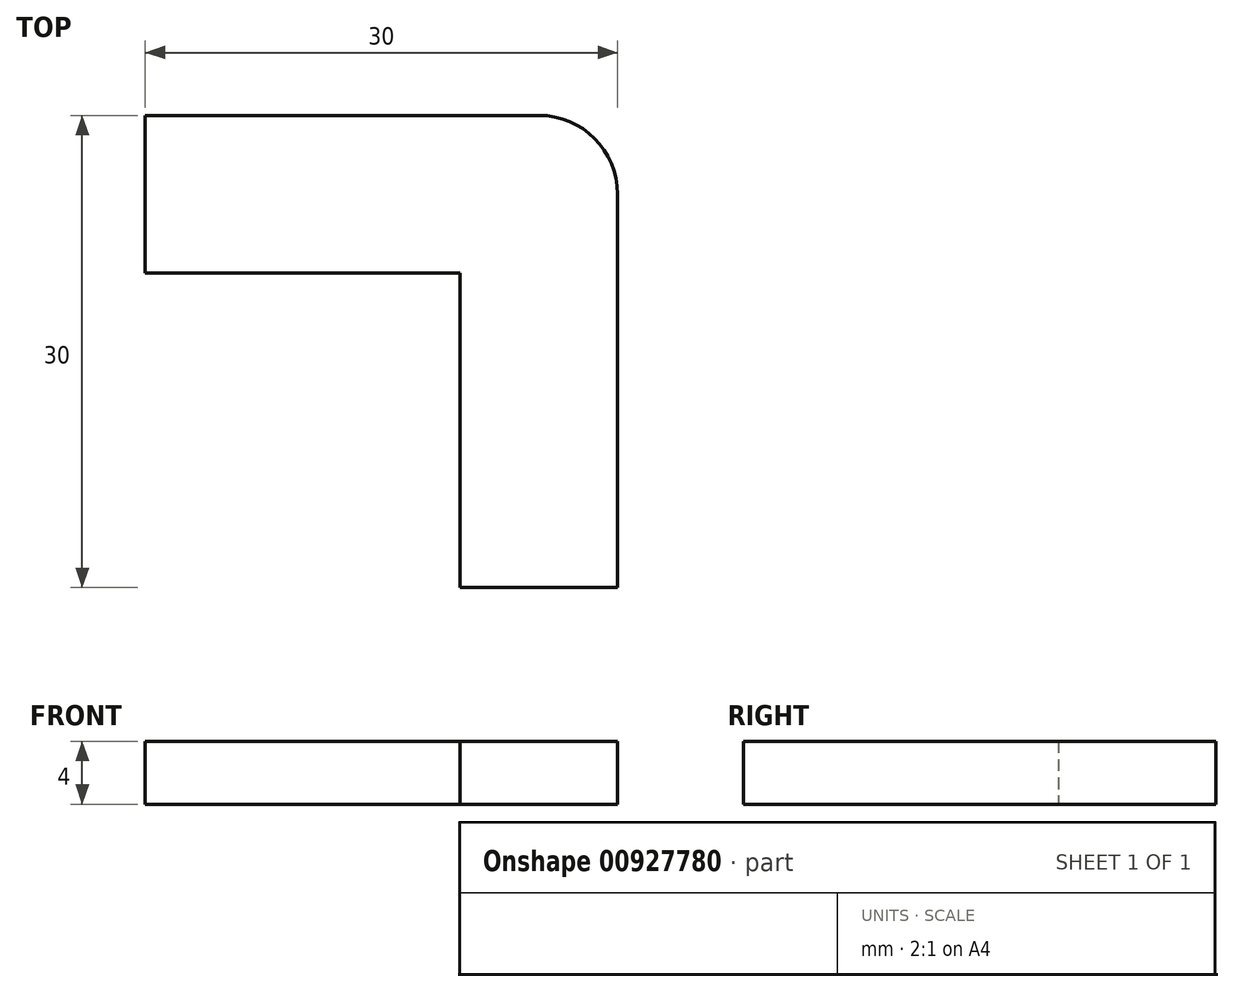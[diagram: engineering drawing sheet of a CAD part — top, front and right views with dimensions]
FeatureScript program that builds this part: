
annotation { "Feature Type Name" : "Feature", "Feature Type Description" : "" }
export const myFeature = defineFeature(function(context is Context, id is Id, definition is map)
    precondition{}
    {
        {
            var Q0;
            Q0=qCreatedBy(makeId("Top.planeOp"),FACE);
            var sketch = newSketch(context, id + "F0", { "sketchPlane" : qUnion([Q0])});
            skLineSegment(sketch, "E0.bottom", {"start": v(5, 15) * mm, "end": v(-5, 15) * mm});
            skLineSegment(sketch, "E0.top", {"start": v(5, -15) * mm, "end": v(-5, -15) * mm});
            skLineSegment(sketch, "E0.left", {"start": v(5, 15) * mm, "end": v(5, -15) * mm});
            skLineSegment(sketch, "E0.right", {"start": v(-5, 15) * mm, "end": v(-5, -15) * mm});
            skPoint(sketch, "E0.middle", {"position": v(0, 0) * mm});
            skLineSegment(sketch, "E1.bottom", {"start": v(-5, 15) * mm, "end": v(-25, 15) * mm});
            skLineSegment(sketch, "E1.top", {"start": v(-5, 5) * mm, "end": v(-25, 5) * mm});
            skLineSegment(sketch, "E1.left", {"start": v(-5, 15) * mm, "end": v(-5, 5) * mm});
            skLineSegment(sketch, "E1.right", {"start": v(-25, 15) * mm, "end": v(-25, 5) * mm});
            skSolve(sketch);
        }
        {
            var Q0;
            Q0=makeQuery(id+"F0.imprint","IMPRINT",FACE,{"disambiguationData":[TD([[makeQuery(id+"F0.imprint","IMPRINT",EDGE,{"derivedFrom":sQuery(id+"F0.wireOp",EDGE,"E0.bottom")}),1.0]])]});
            var Q1;
            Q1=makeQuery(id+"F0.imprint","IMPRINT",FACE,{"disambiguationData":[TD([[makeQuery(id+"F0.imprint","IMPRINT",EDGE,{"derivedFrom":sQuery(id+"F0.wireOp",EDGE,"E1.bottom")}),1.0]])]});
            extrude(context, id + "F1", {"entities" : qUnion([Q0, Q1]), "depth" : 4 * mm, "offsetDistance" : 25.4 * mm});
        }
        {
            var Q0;
            Q0=makeQuery(id+"F1.opExtrude","SWEPT_EDGE",EDGE,{"disambiguationData":[OSD([sQuery(id+"F0.wireOp",EDGE,"E0.bottom"),sQuery(id+"F0.wireOp",EDGE,"E0.left")])]});
            fillet(context, id + "F2", {"entities" : qUnion([Q0]), "radius" : 5 * mm, "tangentPropagation" : true, "allowEdgeOverflow" : false});
        }
    });
